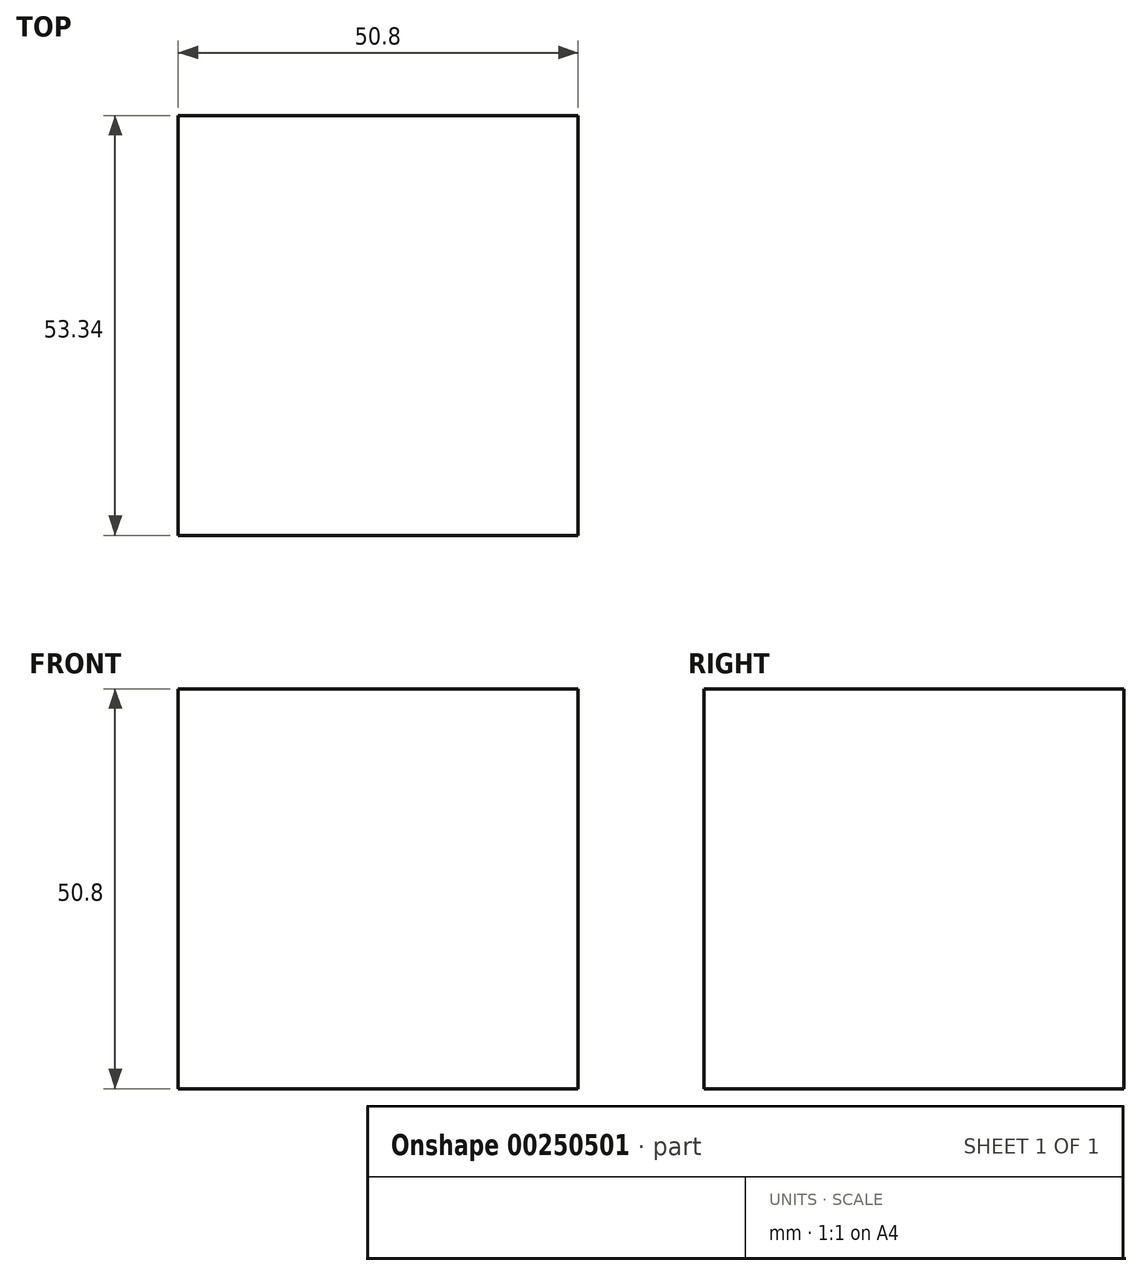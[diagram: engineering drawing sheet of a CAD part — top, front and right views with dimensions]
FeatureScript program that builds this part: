
annotation { "Feature Type Name" : "Feature", "Feature Type Description" : "" }
export const myFeature = defineFeature(function(context is Context, id is Id, definition is map)
    precondition{}
    {
        {
            var Q0;
            Q0=qCreatedBy(makeId("Front.planeOp"),FACE);
            var sketch = newSketch(context, id + "F0", { "sketchPlane" : qUnion([Q0])});
            skLineSegment(sketch, "E0.bottom", {"start": v(-25.4, 25.4) * mm, "end": v(25.4, 25.4) * mm});
            skLineSegment(sketch, "E0.top", {"start": v(-25.4, -25.4) * mm, "end": v(25.4, -25.4) * mm});
            skLineSegment(sketch, "E0.left", {"start": v(-25.4, 25.4) * mm, "end": v(-25.4, -25.4) * mm});
            skLineSegment(sketch, "E0.right", {"start": v(25.4, 25.4) * mm, "end": v(25.4, -25.4) * mm});
            skPoint(sketch, "E0.middle", {"position": v(0, 0) * mm});
            skSolve(sketch);
        }
        {
            var Q0;
            Q0 = qSketchRegion(id + "F0", true);
            extrude(context, id + "F1", {"entities" : qUnion([Q0]), "endBound" : BoundingType.SYMMETRIC, "depth" : 53.34 * mm});
        }
    });
